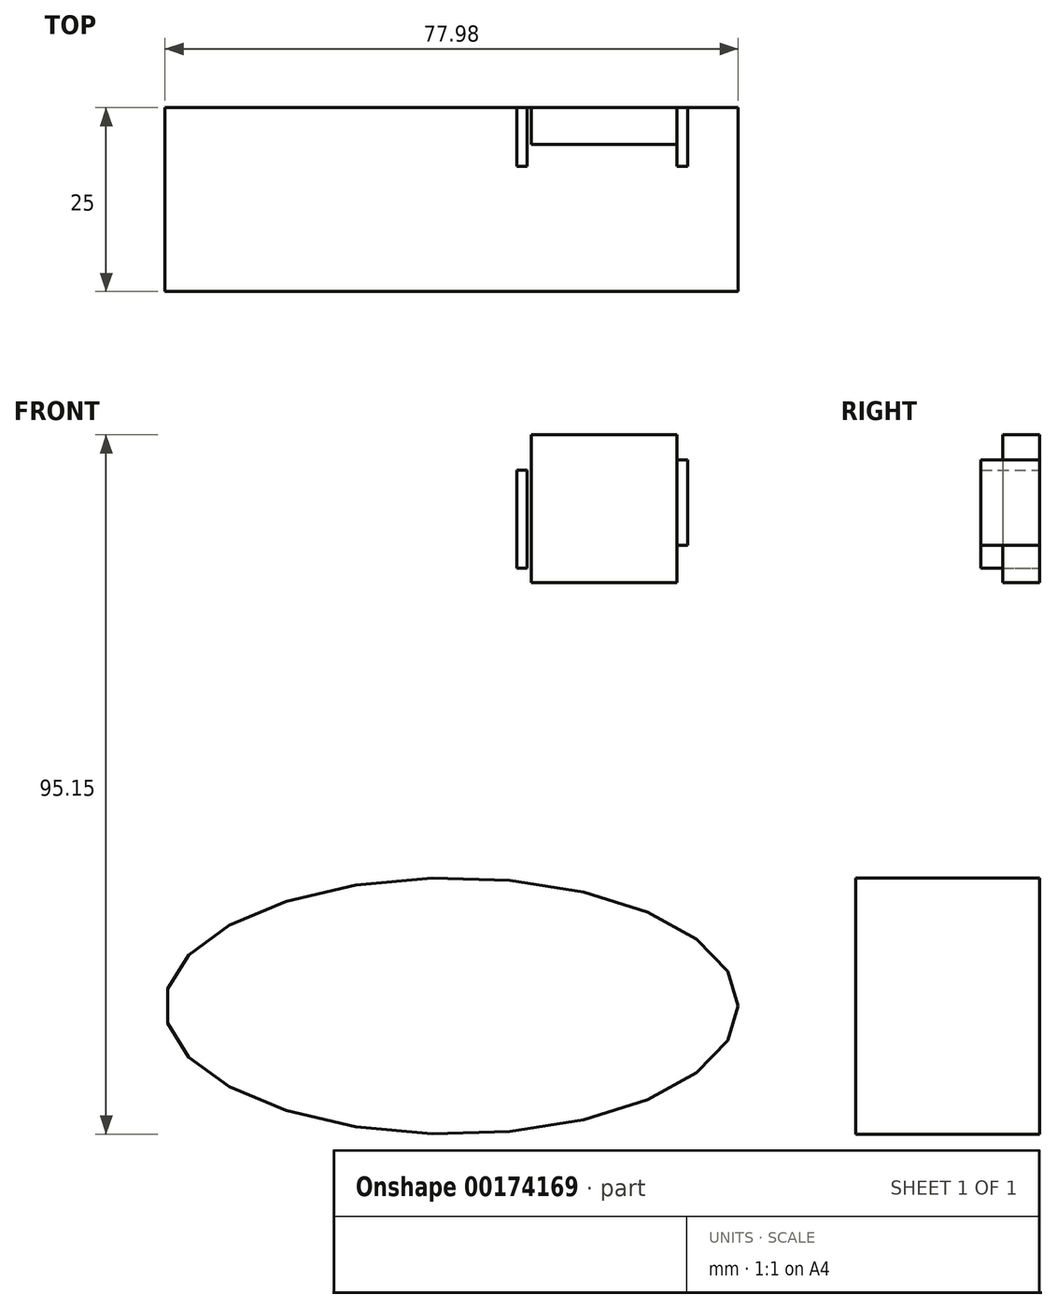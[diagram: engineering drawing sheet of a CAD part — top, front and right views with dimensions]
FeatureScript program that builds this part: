
annotation { "Feature Type Name" : "Feature", "Feature Type Description" : "" }
export const myFeature = defineFeature(function(context is Context, id is Id, definition is map)
    precondition{}
    {
        {
            var Q0;
            Q0=qCreatedBy(makeId("Front.planeOp"),FACE);
            var sketch = newSketch(context, id + "F0", { "sketchPlane" : qUnion([Q0])});
            skLineSegment(sketch, "E0.bottom", {"start": v(-43.62, 58.07) * mm, "end": v(-23.8, 58.07) * mm});
            skLineSegment(sketch, "E0.top", {"start": v(-43.62, 37.96) * mm, "end": v(-23.8, 37.96) * mm});
            skLineSegment(sketch, "E0.left", {"start": v(-43.62, 58.07) * mm, "end": v(-43.62, 37.96) * mm});
            skLineSegment(sketch, "E0.right", {"start": v(-23.8, 58.07) * mm, "end": v(-23.8, 37.96) * mm});
            skSolve(sketch);
        }
        {
            var Q0;
            Q0=makeQuery(id+"F0.imprint","IMPRINT",FACE,{"disambiguationData":[TD([[makeQuery(id+"F0.imprint","IMPRINT",EDGE,{"derivedFrom":sQuery(id+"F0.wireOp",EDGE,"E0.bottom")}),-1.0]])]});
            extrude(context, id + "F1", {"entities" : qUnion([Q0]), "depth" : 5 * mm});
        }
        {
            var Q0;
            Q0=qCreatedBy(makeId("Front.planeOp"),FACE);
            var sketch = newSketch(context, id + "F2", { "sketchPlane" : qUnion([Q0])});
            skLineSegment(sketch, "E1.bottom", {"start": v(-23.8, 54.67) * mm, "end": v(-22.38, 54.67) * mm});
            skLineSegment(sketch, "E1.top", {"start": v(-23.8, 43.06) * mm, "end": v(-22.38, 43.06) * mm});
            skLineSegment(sketch, "E1.left", {"start": v(-23.8, 54.67) * mm, "end": v(-23.8, 43.06) * mm});
            skLineSegment(sketch, "E1.right", {"start": v(-22.38, 54.67) * mm, "end": v(-22.38, 43.06) * mm});
            skLineSegment(sketch, "E2.bottom", {"start": v(-44.2, 53.26) * mm, "end": v(-45.6, 53.26) * mm});
            skLineSegment(sketch, "E2.top", {"start": v(-44.2, 39.94) * mm, "end": v(-45.6, 39.94) * mm});
            skLineSegment(sketch, "E2.left", {"start": v(-44.2, 53.26) * mm, "end": v(-44.2, 39.94) * mm});
            skLineSegment(sketch, "E2.right", {"start": v(-45.6, 53.26) * mm, "end": v(-45.6, 39.94) * mm});
            skSolve(sketch);
        }
        {
            var Q0;
            Q0=makeQuery(id+"F2.imprint","IMPRINT",FACE,{"disambiguationData":[TD([[makeQuery(id+"F2.imprint","IMPRINT",EDGE,{"derivedFrom":sQuery(id+"F2.wireOp",EDGE,"E1.bottom")}),-1.0]])]});
            var Q1;
            Q1=makeQuery(id+"F2.imprint","IMPRINT",FACE,{"disambiguationData":[TD([[makeQuery(id+"F2.imprint","IMPRINT",EDGE,{"derivedFrom":sQuery(id+"F2.wireOp",EDGE,"E2.bottom")}),1.0]])]});
            extrude(context, id + "F3", {"entities" : qUnion([Q0, Q1]), "operationType" : NewBodyOperationType.ADD, "depth" : 8 * mm});
        }
        {
            var Q0;
            Q0=qCreatedBy(makeId("Front.planeOp"),FACE);
            var sketch = newSketch(context, id + "F4", { "sketchPlane" : qUnion([Q0])});
            skEllipse(sketch, "E3", {"center": v(-54.46, -19.65) * mm, "majorRadius": 38.99 * mm, "minorRadius": 17.44 * mm, "majorAxis": v(1, 0)});
            skSolve(sketch);
        }
        {
            var Q0;
            Q0 = qSketchRegion(id + "F4", true);
            extrude(context, id + "F5", {"entities" : qUnion([Q0]), "depth" : 25 * mm});
        }
        {
            var Q0;
            Q0=makeQuery(id+"F5.opExtrude","CAP_FACE",FACE,{"disambiguationData":[OSD([sQuery(id+"F4.wireOp",EDGE,"E3")])],"isStart":false});
            var sketch = newSketch(context, id + "F6", { "sketchPlane" : qUnion([Q0])});
            skSolve(sketch);
        }
        {
            var Q0;
            Q0=makeQuery(id+"F6.imprint","IMPRINT",FACE,{"disambiguationData":[TD([[makeQuery(id+"F6.imprint","IMPRINT",EDGE,{"derivedFrom":makeQuery(id+"F5.opExtrude","CAP_EDGE",EDGE,{"disambiguationData":[OSD([sQuery(id+"F4.wireOp",EDGE,"E3")])],"isStart":false})}),1.0]])]});
            extrude(context, id + "F7", {"entities" : qUnion([Q0]), "operationType" : NewBodyOperationType.ADD, "oppositeDirection" : true, "depth" : 1 * mm});
        }
    });
